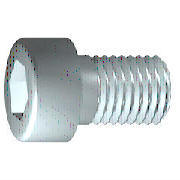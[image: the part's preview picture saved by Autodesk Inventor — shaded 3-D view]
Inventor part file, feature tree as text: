
AUTODESK INVENTOR PART (.ipt)
format: ipt  version: 2015 (Build 190159000, 159)  size: 193,536 bytes
history: native  units: mm (DEFAULTED — no unit token found)
features: sketch x2, extrude x1, plane x1, fillet x1
ambient origin geometry x7: Origin, YZ Plane, XY Plane, X Axis, Y Axis, Z Axis, Center Point
bodies: Solid1 (feature_tree), Body (feature_tree)
feature tree (5):
  extrude  "Slot"  Depth=3.5052mm
  plane  "Work Plane1"
  fillet  "Fillet2"  Radius=3.5052mm
  sketch  "Sketch1"  dims[d1=5.952798mm d2=1.984602mm d3=3.5052mm]
  sketch  "Sketch2"  dims[d4=1.6256mm d5=60.0deg d6=3.5052mm d7=3.5052mm d8=3.196904mm d9=5.7404mm d10=90.0deg d11=10.0mm d12=0.0mm d13=5.952798mm d14=0.0mm d15=0.47244mm d16=0.47244mm d17=0.3302mm d19=0.0mm d26=7.9375mm d27=45.0deg d28=0.0mm d29=0.0mm d30=0.127mm]
